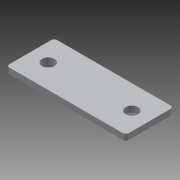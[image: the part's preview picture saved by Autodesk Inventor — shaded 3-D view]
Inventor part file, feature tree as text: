
AUTODESK INVENTOR PART (.ipt)
format: ipt  version: 2014 SP1 (Build 180222100, 222)  size: 87,040 bytes
history: native  units: in
note: dims shown in document units (in); Inventor stores cm internally (conversion verified against a paired STEP export)
features: extrude x1, fillet x1, sketch x1
ambient origin geometry x8: Origin, YZ Plane, XZ Plane, XY Plane, X Axis, Y Axis, Z Axis, Center Point
bodies: Solid1 (feature_tree)
feature tree (3):
  extrude  "Extrusion1"  Depth=1.0in
  fillet  "Fillet1"  Radius=1.75in
  sketch  "Sketch1"  dims[d0=2.5in d2=1.0in d3=1.75in d4=0.26in d5=0.125in d6=0.0in d7=0.0625in]
